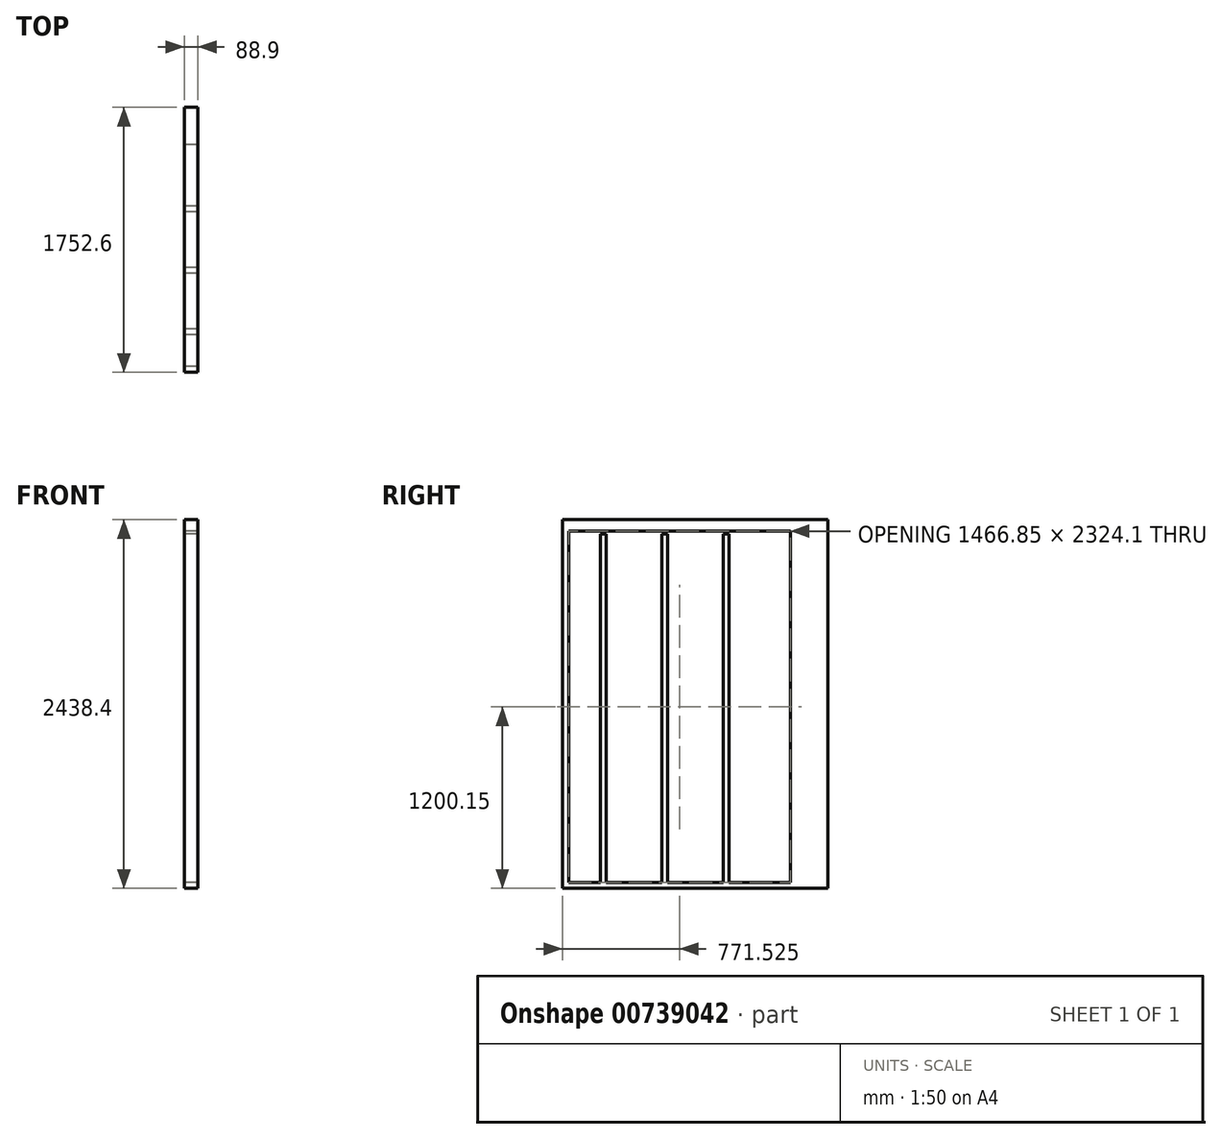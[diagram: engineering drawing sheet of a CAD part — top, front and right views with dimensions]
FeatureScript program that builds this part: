
annotation { "Feature Type Name" : "Feature", "Feature Type Description" : "" }
export const myFeature = defineFeature(function(context is Context, id is Id, definition is map)
    precondition{}
    {
        {
            var Q0;
            Q0=qCreatedBy(makeId("Right.planeOp"),FACE);
            var sketch = newSketch(context, id + "F0", { "sketchPlane" : qUnion([Q0])});
            skLineSegment(sketch, "E0.bottom", {"start": v(0, 0) * mm, "end": v(1752.6, 0) * mm});
            skLineSegment(sketch, "E0.top", {"start": v(0, 2438.4) * mm, "end": v(1752.6, 2438.4) * mm});
            skLineSegment(sketch, "E0.left", {"start": v(0, 0) * mm, "end": v(0, 2438.4) * mm});
            skLineSegment(sketch, "E1", {"start": v(1752.6, 2400.3) * mm, "end": v(1752.6, 2438.4) * mm});
            skLineSegment(sketch, "E2", {"start": v(1752.6, 38.1) * mm, "end": v(1752.6, 0) * mm});
            skLineSegment(sketch, "E3.bottom", {"start": v(247.65, 2344.2) * mm, "end": v(285.75, 2344.2) * mm});
            skLineSegment(sketch, "E3.top", {"start": v(247.65, 38.1) * mm, "end": v(285.75, 38.1) * mm});
            skLineSegment(sketch, "E3.left", {"start": v(247.65, 2344.2) * mm, "end": v(247.65, 38.1) * mm});
            skLineSegment(sketch, "E3.right", {"start": v(285.75, 2344.2) * mm, "end": v(285.75, 38.1) * mm});
            skLineSegment(sketch, "E4.bottom", {"start": v(654.05, 2344.2) * mm, "end": v(692.15, 2344.2) * mm});
            skLineSegment(sketch, "E4.top", {"start": v(654.05, 38.1) * mm, "end": v(692.15, 38.1) * mm});
            skLineSegment(sketch, "E4.left", {"start": v(654.05, 2344.2) * mm, "end": v(654.05, 38.1) * mm});
            skLineSegment(sketch, "E4.right", {"start": v(692.15, 2344.2) * mm, "end": v(692.15, 38.1) * mm});
            skLineSegment(sketch, "E5.bottom", {"start": v(1060.45, 2344.2) * mm, "end": v(1098.55, 2344.2) * mm});
            skLineSegment(sketch, "E5.top", {"start": v(1060.45, 38.1) * mm, "end": v(1098.55, 38.1) * mm});
            skLineSegment(sketch, "E5.left", {"start": v(1060.45, 2344.2) * mm, "end": v(1060.45, 38.1) * mm});
            skLineSegment(sketch, "E5.right", {"start": v(1098.55, 2344.2) * mm, "end": v(1098.55, 38.1) * mm});
            skLineSegment(sketch, "E6.bottom", {"start": v(1504.95, 2362.2) * mm, "end": v(1574.8, 2362.2) * mm});
            skLineSegment(sketch, "E6.top", {"start": v(1466.85, 38.1) * mm, "end": v(1612.9, 38.1) * mm});
            skLineSegment(sketch, "E7", {"start": v(1752.6, 38.1) * mm, "end": v(0, 38.1) * mm});
            skLineSegment(sketch, "E8", {"start": v(1752.6, 2400.3) * mm, "end": v(0, 2400.3) * mm});
            skLineSegment(sketch, "E9.top", {"start": v(1752.6, 2362.2) * mm, "end": v(0, 2362.2) * mm});
            skLineSegment(sketch, "E9.left", {"start": v(1752.6, 2400.3) * mm, "end": v(1752.6, 2362.2) * mm});
            skLineSegment(sketch, "E9.right", {"start": v(0, 2400.3) * mm, "end": v(0, 2362.2) * mm});
            skLineSegment(sketch, "E10.bottom", {"start": v(215.9, 2362.2) * mm, "end": v(183.93, 2362.2) * mm});
            skLineSegment(sketch, "E10.top", {"start": v(222.03, 38.1) * mm, "end": v(177.8, 38.1) * mm});
            skLineSegment(sketch, "E11.bottom", {"start": v(0, 2362.2) * mm, "end": v(38.1, 2362.2) * mm});
            skLineSegment(sketch, "E11.top", {"start": v(0, 38.1) * mm, "end": v(38.1, 38.1) * mm});
            skLineSegment(sketch, "E11.left", {"start": v(0, 2362.2) * mm, "end": v(0, 38.1) * mm});
            skLineSegment(sketch, "E11.right", {"start": v(38.1, 2362.2) * mm, "end": v(38.1, 38.1) * mm});
            skLineSegment(sketch, "E12.bottom", {"start": v(215.9, 2362.2) * mm, "end": v(177.8, 2362.2) * mm});
            skLineSegment(sketch, "E12.top", {"start": v(215.9, 38.1) * mm, "end": v(177.8, 38.1) * mm});
            skLineSegment(sketch, "E13.bottom", {"start": v(1752.6, 2362.2) * mm, "end": v(1714.5, 2362.2) * mm});
            skLineSegment(sketch, "E13.top", {"start": v(1752.6, 38.1) * mm, "end": v(1714.5, 38.1) * mm});
            skLineSegment(sketch, "E13.left", {"start": v(1752.6, 2362.2) * mm, "end": v(1752.6, 38.1) * mm});
            skLineSegment(sketch, "E13.right", {"start": v(1714.5, 2362.2) * mm, "end": v(1714.5, 38.1) * mm});
            skLineSegment(sketch, "E14.bottom", {"start": v(1504.95, 2362.2) * mm, "end": v(1466.85, 2362.2) * mm});
            skLineSegment(sketch, "E14.top", {"start": v(1504.95, 38.1) * mm, "end": v(1466.85, 38.1) * mm});
            skLineSegment(sketch, "E14.left", {"start": v(1504.95, 2362.2) * mm, "end": v(1504.95, 38.1) * mm});
            skLineSegment(sketch, "E14.right", {"start": v(1466.85, 2362.2) * mm, "end": v(1466.85, 38.1) * mm});
            skSolve(sketch);
        }
        {
            var Q0;
            Q0 = qSketchRegion(id + "F0", true);
            var Q1;
            Q1=makeQuery(id+"F0.imprint","IMPRINT",FACE,{"disambiguationData":[TD([[makeQuery(id+"F0.imprint","IMPRINT",EDGE,{"derivedFrom":sQuery(id+"F0.wireOp",EDGE,"E3.bottom")}),-1.0]])]});
            var Q2;
            Q2=makeQuery(id+"F0.imprint","IMPRINT",FACE,{"disambiguationData":[TD([[makeQuery(id+"F0.imprint","IMPRINT",EDGE,{"derivedFrom":sQuery(id+"F0.wireOp",EDGE,"E4.bottom")}),-1.0]])]});
            var Q3;
            Q3=makeQuery(id+"F0.imprint","IMPRINT",FACE,{"disambiguationData":[TD([[makeQuery(id+"F0.imprint","IMPRINT",EDGE,{"derivedFrom":sQuery(id+"F0.wireOp",EDGE,"E5.bottom")}),-1.0]])]});
            var Q4;
            Q4=makeQuery(id+"F0.imprint","IMPRINT",FACE,{"disambiguationData":[TD([[makeQuery(id+"F0.imprint","IMPRINT",EDGE,{"derivedFrom":sQuery(id+"F0.wireOp",EDGE,"E6.bottom")}),-1.0]])]});
            var Q5;
            Q5=makeQuery(id+"F0.imprint","IMPRINT",FACE,{"disambiguationData":[TD([[makeQuery(id+"F0.imprint","IMPRINT",EDGE,{"derivedFrom":sQuery(id+"F0.wireOp",EDGE,"E14.bottom")}),1.0]])]});
            extrude(context, id + "F1", {"entities" : qUnion([Q0, Q1, Q2, Q3, Q4, Q5]), "depth" : 88.9 * mm, "offsetDistance" : 25.4 * mm});
        }
    });
